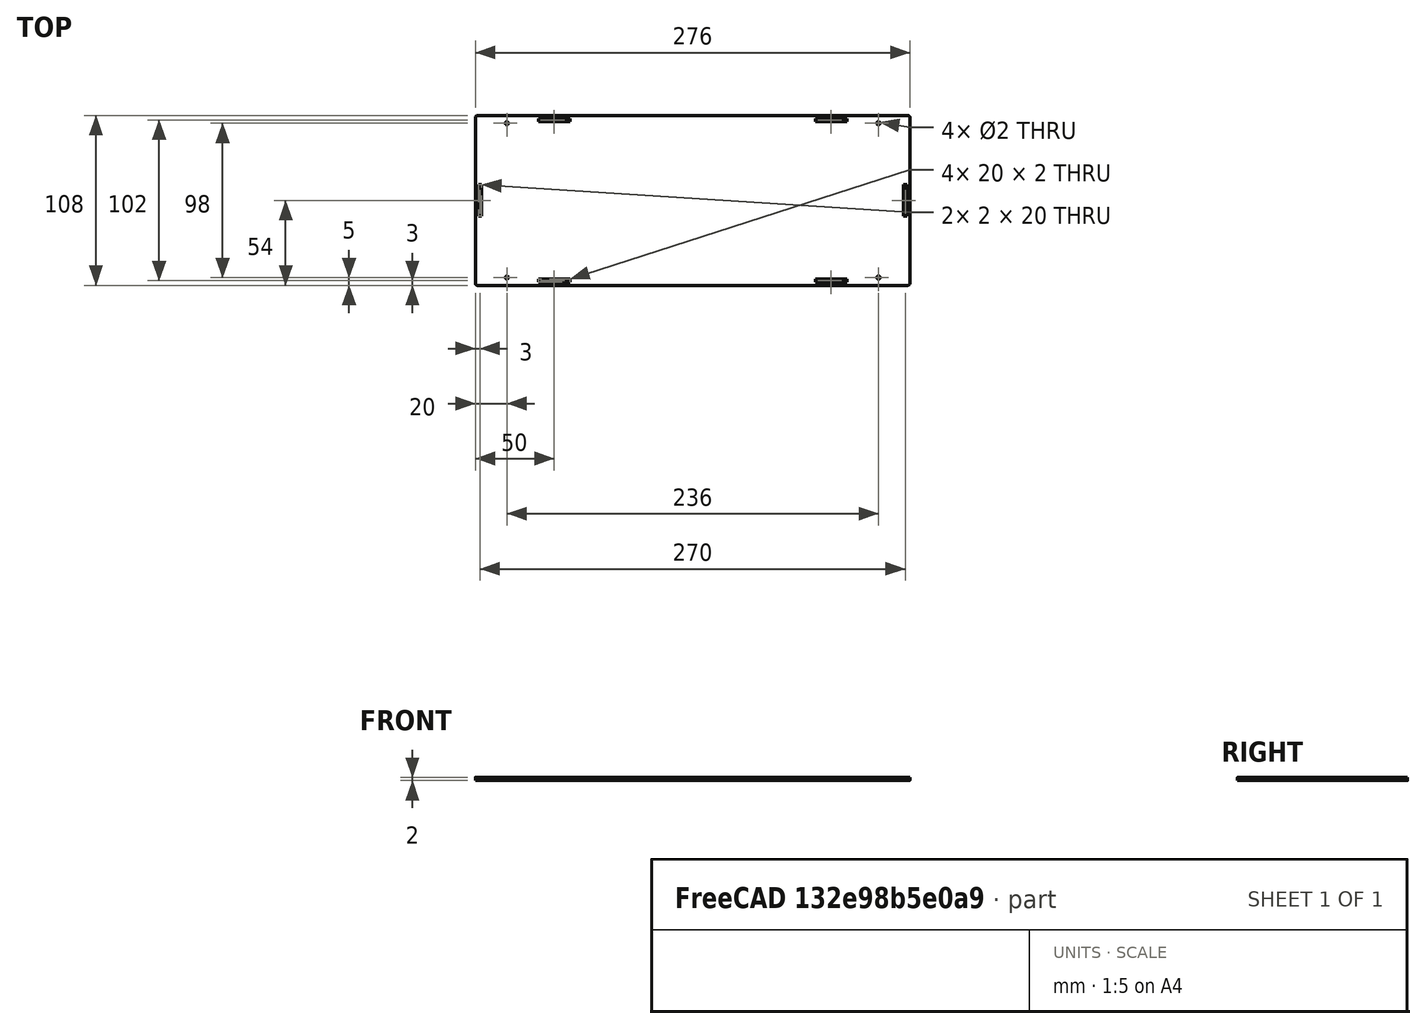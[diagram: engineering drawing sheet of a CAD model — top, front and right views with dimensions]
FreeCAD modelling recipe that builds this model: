
FCSTD DOCUMENT  (FreeCAD 0.19R24291 (Git))
Label: keyboard-pc
License: All rights reserved
LicenseURL: http://en.wikipedia.org/wiki/All_rights_reserved
objects: Sketcher::SketchObject×1, PartDesign::Pad×1, PartDesign::Body×1
note: 4 computed .brp shape members not serialized (recipe doc carries the construction recipe); baked Part::Feature solids carry a one-line shape summary decoded from their .brp

FEATURE [Sketcher::SketchObject] Sketch  label="keyboard-up"
  FullyConstrained = false
  MapMode = 5
  Support = -> [XY_Plane]
  sketch-geometry (176):
    g0: LineSegment StartX=-136.5 StartY=54 StartZ=0 EndX=136.5 EndY=54 EndZ=0
    g1: LineSegment StartX=138 StartY=52.5 StartZ=0 EndX=138 EndY=-52.5 EndZ=0
    g2: LineSegment StartX=136.5 StartY=-54 StartZ=0 EndX=-136.5 EndY=-54 EndZ=0
    g3: LineSegment StartX=-138 StartY=-52.5 StartZ=0 EndX=-138 EndY=52.5 EndZ=0
    g4: Circle CenterX=-118 CenterY=-49 CenterZ=0 NormalX=0 NormalY=0 NormalZ=1 AngleXU=0 Radius=1
    g5: Circle CenterX=118 CenterY=-49 CenterZ=0 NormalX=0 NormalY=0 NormalZ=1 AngleXU=0 Radius=1
    g6: Circle CenterX=-118 CenterY=49 CenterZ=0 NormalX=0 NormalY=0 NormalZ=1 AngleXU=0 Radius=1
    g7: Circle CenterX=118 CenterY=49 CenterZ=0 NormalX=0 NormalY=0 NormalZ=1 AngleXU=0 Radius=1
    g8: LineSegment StartX=-98 StartY=-50 StartZ=0 EndX=-78 EndY=-50 EndZ=0
    g9: LineSegment StartX=-78 StartY=-50 StartZ=0 EndX=-78 EndY=-52 EndZ=0
    g10: LineSegment StartX=-78 StartY=-52 StartZ=0 EndX=-98 EndY=-52 EndZ=0
    g11: LineSegment StartX=-98 StartY=-52 StartZ=0 EndX=-98 EndY=-50 EndZ=0
    g12: LineSegment StartX=-98 StartY=52 StartZ=0 EndX=-78 EndY=52 EndZ=0
    g13: LineSegment StartX=-78 StartY=52 StartZ=0 EndX=-78 EndY=50 EndZ=0
    g14: LineSegment StartX=-78 StartY=50 StartZ=0 EndX=-98 EndY=50 EndZ=0
    g15: LineSegment StartX=-98 StartY=50 StartZ=0 EndX=-98 EndY=52 EndZ=0
    g16: LineSegment StartX=78 StartY=52 StartZ=0 EndX=98 EndY=52 EndZ=0
    g17: LineSegment StartX=98 StartY=52 StartZ=0 EndX=98 EndY=50 EndZ=0
    g18: LineSegment StartX=98 StartY=50 StartZ=0 EndX=78 EndY=50 EndZ=0
    g19: LineSegment StartX=78 StartY=50 StartZ=0 EndX=78 EndY=52 EndZ=0
    g20: LineSegment StartX=78 StartY=-50 StartZ=0 EndX=98 EndY=-50 EndZ=0
    g21: LineSegment StartX=98 StartY=-50 StartZ=0 EndX=98 EndY=-52 EndZ=0
    g22: LineSegment StartX=98 StartY=-52 StartZ=0 EndX=78 EndY=-52 EndZ=0
    g23: LineSegment StartX=78 StartY=-52 StartZ=0 EndX=78 EndY=-50 EndZ=0
    g24: LineSegment StartX=-136 StartY=10 StartZ=0 EndX=-134 EndY=10 EndZ=0
    g25: LineSegment StartX=-134 StartY=10 StartZ=0 EndX=-134 EndY=-10 EndZ=0
    g26: LineSegment StartX=-134 StartY=-10 StartZ=0 EndX=-136 EndY=-10 EndZ=0
    g27: LineSegment StartX=-136 StartY=-10 StartZ=0 EndX=-136 EndY=10 EndZ=0
    g28: LineSegment StartX=134 StartY=10 StartZ=0 EndX=136 EndY=10 EndZ=0
    g29: LineSegment StartX=136 StartY=10 StartZ=0 EndX=136 EndY=-10 EndZ=0
    g30: LineSegment StartX=136 StartY=-10 StartZ=0 EndX=134 EndY=-10 EndZ=0
    g31: LineSegment StartX=134 StartY=-10 StartZ=0 EndX=134 EndY=10 EndZ=0
    g32: ArcOfCircle CenterX=-136.5 CenterY=-52.5 CenterZ=0 NormalX=0 NormalY=0 NormalZ=1 AngleXU=0 Radius=1.5 StartAngle=3.14159 EndAngle=4.71239
    g33: ArcOfCircle CenterX=-136.5 CenterY=52.5 CenterZ=0 NormalX=0 NormalY=0 NormalZ=1 AngleXU=0 Radius=1.5 StartAngle=1.5708 EndAngle=3.14159
    g34: ArcOfCircle CenterX=136.5 CenterY=52.5 CenterZ=0 NormalX=0 NormalY=0 NormalZ=1 AngleXU=0 Radius=1.5 StartAngle=-1.8e-15 EndAngle=1.5708
    g35: ArcOfCircle CenterX=136.5 CenterY=-52.5 CenterZ=0 NormalX=0 NormalY=0 NormalZ=1 AngleXU=0 Radius=1.5 StartAngle=4.71239 EndAngle=6.28319
    g36: LineSegment StartX=-118 StartY=44 StartZ=0 EndX=-82 EndY=44 EndZ=0
    g37: LineSegment StartX=-82 StartY=44 StartZ=0 EndX=-82 EndY=42 EndZ=0
    g38: LineSegment StartX=-82 StartY=42 StartZ=0 EndX=-118 EndY=42 EndZ=0
    g39: LineSegment StartX=-118 StartY=42 StartZ=0 EndX=-118 EndY=44 EndZ=0
    g40: Circle CenterX=44 CenterY=30.5 CenterZ=0 NormalX=0 NormalY=0 NormalZ=1 AngleXU=0 Radius=1.5
    g41: Circle CenterX=44 CenterY=-30.5 CenterZ=0 NormalX=0 NormalY=0 NormalZ=1 AngleXU=0 Radius=1.5
    g42: Circle CenterX=120 CenterY=30.5 CenterZ=0 NormalX=0 NormalY=0 NormalZ=1 AngleXU=0 Radius=1.5
    g43: Circle CenterX=120 CenterY=-30.5 CenterZ=0 NormalX=0 NormalY=0 NormalZ=1 AngleXU=0 Radius=1.5
    g44: Circle CenterX=34 CenterY=30.5 CenterZ=0 NormalX=0 NormalY=0 NormalZ=1 AngleXU=0 Radius=1.5
    g45: Circle CenterX=34 CenterY=-30.5 CenterZ=0 NormalX=0 NormalY=0 NormalZ=1 AngleXU=0 Radius=1.5
    g46: Circle CenterX=110 CenterY=30.5 CenterZ=0 NormalX=0 NormalY=0 NormalZ=1 AngleXU=0 Radius=1.5
    g47: Circle CenterX=110 CenterY=-30.5 CenterZ=0 NormalX=0 NormalY=0 NormalZ=1 AngleXU=0 Radius=1.5
    g48: Circle CenterX=-111.5 CenterY=-48.5 CenterZ=0 NormalX=0 NormalY=0 NormalZ=1 AngleXU=0 Radius=1.5
    g49: Circle CenterX=-111.5 CenterY=48.5 CenterZ=0 NormalX=0 NormalY=0 NormalZ=1 AngleXU=0 Radius=1.5
    g50: Circle CenterX=111.5 CenterY=-48.5 CenterZ=0 NormalX=0 NormalY=0 NormalZ=1 AngleXU=0 Radius=1.5
    g51: Circle CenterX=111.5 CenterY=48.5 CenterZ=0 NormalX=0 NormalY=0 NormalZ=1 AngleXU=0 Radius=1.5
    g52: Circle CenterX=-130 CenterY=-39 CenterZ=0 NormalX=0 NormalY=0 NormalZ=1 AngleXU=0 Radius=1
    g53: Circle CenterX=7.5 CenterY=-37 CenterZ=0 NormalX=0 NormalY=0 NormalZ=1 AngleXU=0 Radius=1
    g54: Circle CenterX=-128 CenterY=21 CenterZ=0 NormalX=0 NormalY=0 NormalZ=1 AngleXU=0 Radius=1
    g55: Circle CenterX=-43.5 CenterY=32 CenterZ=0 NormalX=0 NormalY=0 NormalZ=1 AngleXU=0 Radius=1.5
    g56: ArcOfCircle CenterX=-112.237 CenterY=33 CenterZ=0 NormalX=0 NormalY=0 NormalZ=1 AngleXU=0 Radius=1.5 StartAngle=5e-16 EndAngle=3.14159
    g57: ArcOfCircle CenterX=-112.237 CenterY=-33 CenterZ=0 NormalX=0 NormalY=0 NormalZ=1 AngleXU=0 Radius=1.5 StartAngle=3.14159 EndAngle=6.28319
    g58: LineSegment StartX=-113.737 StartY=33 StartZ=0 EndX=-113.737 EndY=-33 EndZ=0
    g59: LineSegment StartX=-110.737 StartY=33 StartZ=0 EndX=-110.737 EndY=-33 EndZ=0
    g60: ArcOfCircle CenterX=-106.237 CenterY=33 CenterZ=0 NormalX=0 NormalY=0 NormalZ=1 AngleXU=0 Radius=1.5 StartAngle=5e-16 EndAngle=3.14159
    g61: ArcOfCircle CenterX=-106.237 CenterY=-33 CenterZ=0 NormalX=0 NormalY=0 NormalZ=1 AngleXU=0 Radius=1.5 StartAngle=3.14159 EndAngle=6.28319
    g62: LineSegment StartX=-107.737 StartY=33 StartZ=0 EndX=-107.737 EndY=-33 EndZ=0
    g63: LineSegment StartX=-104.737 StartY=33 StartZ=0 EndX=-104.737 EndY=-33 EndZ=0
    g64: ArcOfCircle CenterX=-94.2366 CenterY=33 CenterZ=0 NormalX=0 NormalY=0 NormalZ=1 AngleXU=0 Radius=1.5 StartAngle=0 EndAngle=3.14159
    g65: ArcOfCircle CenterX=-94.2366 CenterY=-33 CenterZ=0 NormalX=0 NormalY=0 NormalZ=1 AngleXU=0 Radius=1.5 StartAngle=3.14159 EndAngle=6.28319
    g66: LineSegment StartX=-95.7366 StartY=33 StartZ=0 EndX=-95.7366 EndY=-33 EndZ=0
    g67: LineSegment StartX=-92.7366 StartY=33 StartZ=0 EndX=-92.7366 EndY=-33 EndZ=0
    g68: ArcOfCircle CenterX=-88.2366 CenterY=33 CenterZ=0 NormalX=0 NormalY=0 NormalZ=1 AngleXU=0 Radius=1.5 StartAngle=5e-16 EndAngle=3.14159
    g69: ArcOfCircle CenterX=-88.2366 CenterY=-33 CenterZ=0 NormalX=0 NormalY=0 NormalZ=1 AngleXU=0 Radius=1.5 StartAngle=3.14159 EndAngle=6.28319
    g70: LineSegment StartX=-89.7366 StartY=33 StartZ=0 EndX=-89.7366 EndY=-33 EndZ=0
    g71: LineSegment StartX=-86.7366 StartY=33 StartZ=0 EndX=-86.7366 EndY=-33 EndZ=0
    g72: ArcOfCircle CenterX=-76.2366 CenterY=33 CenterZ=0 NormalX=0 NormalY=0 NormalZ=1 AngleXU=0 Radius=1.5 StartAngle=2.2e-15 EndAngle=3.14159
    g73: ArcOfCircle CenterX=-76.2366 CenterY=-33 CenterZ=0 NormalX=0 NormalY=0 NormalZ=1 AngleXU=0 Radius=1.5 StartAngle=3.14159 EndAngle=6.28319
    g74: LineSegment StartX=-77.7366 StartY=33 StartZ=0 EndX=-77.7366 EndY=-33 EndZ=0
    g75: LineSegment StartX=-74.7366 StartY=33 StartZ=0 EndX=-74.7366 EndY=-33 EndZ=0
    g76: ArcOfCircle CenterX=-70.2366 CenterY=33 CenterZ=0 NormalX=0 NormalY=0 NormalZ=1 AngleXU=0 Radius=1.5 StartAngle=5e-16 EndAngle=3.14159
    g77: ArcOfCircle CenterX=-70.2366 CenterY=-33 CenterZ=0 NormalX=0 NormalY=0 NormalZ=1 AngleXU=0 Radius=1.5 StartAngle=3.14159 EndAngle=6.28319
    g78: LineSegment StartX=-71.7366 StartY=33 StartZ=0 EndX=-71.7366 EndY=-33 EndZ=0
    g79: LineSegment StartX=-68.7366 StartY=33 StartZ=0 EndX=-68.7366 EndY=-33 EndZ=0
    g80: ArcOfCircle CenterX=-58.2366 CenterY=33 CenterZ=0 NormalX=0 NormalY=0 NormalZ=1 AngleXU=0 Radius=1.5 StartAngle=0 EndAngle=3.14159
    g81: ArcOfCircle CenterX=-58.2366 CenterY=-33 CenterZ=0 NormalX=0 NormalY=0 NormalZ=1 AngleXU=0 Radius=1.5 StartAngle=3.14159 EndAngle=6.28319
    g82: LineSegment StartX=-59.7366 StartY=33 StartZ=0 EndX=-59.7366 EndY=-33 EndZ=0
    g83: LineSegment StartX=-56.7366 StartY=33 StartZ=0 EndX=-56.7366 EndY=-33 EndZ=0
    g84: ArcOfCircle CenterX=-52.2366 CenterY=33 CenterZ=0 NormalX=0 NormalY=0 NormalZ=1 AngleXU=0 Radius=1.5 StartAngle=1.9e-15 EndAngle=3.14159
    g85: ArcOfCircle CenterX=-52.2366 CenterY=-33 CenterZ=0 NormalX=0 NormalY=0 NormalZ=1 AngleXU=0 Radius=1.5 StartAngle=3.14159 EndAngle=6.28319
    g86: LineSegment StartX=-53.7366 StartY=33 StartZ=0 EndX=-53.7366 EndY=-33 EndZ=0
    g87: LineSegment StartX=-50.7366 StartY=33 StartZ=0 EndX=-50.7366 EndY=-33 EndZ=0
    g88: ArcOfCircle CenterX=-40.2366 CenterY=33 CenterZ=0 NormalX=0 NormalY=0 NormalZ=1 AngleXU=0 Radius=1.5 StartAngle=1.9e-15 EndAngle=3.14159
    g89: ArcOfCircle CenterX=-40.2366 CenterY=-33 CenterZ=0 NormalX=0 NormalY=0 NormalZ=1 AngleXU=0 Radius=1.5 StartAngle=3.14159 EndAngle=6.28319
    g90: LineSegment StartX=-41.7366 StartY=33 StartZ=0 EndX=-41.7366 EndY=-33 EndZ=0
    g91: LineSegment StartX=-38.7366 StartY=33 StartZ=0 EndX=-38.7366 EndY=-33 EndZ=0
    g92: ArcOfCircle CenterX=-34.2366 CenterY=33 CenterZ=0 NormalX=0 NormalY=0 NormalZ=1 AngleXU=0 Radius=1.5 StartAngle=-1.8e-15 EndAngle=3.14159
    g93: ArcOfCircle CenterX=-34.2366 CenterY=-33 CenterZ=0 NormalX=0 NormalY=0 NormalZ=1 AngleXU=0 Radius=1.5 StartAngle=3.14159 EndAngle=6.28319
    g94: LineSegment StartX=-35.7366 StartY=33 StartZ=0 EndX=-35.7366 EndY=-33 EndZ=0
    g95: LineSegment StartX=-32.7366 StartY=33 StartZ=0 EndX=-32.7366 EndY=-33 EndZ=0
    g96: ArcOfCircle CenterX=-22.2366 CenterY=33 CenterZ=0 NormalX=0 NormalY=0 NormalZ=1 AngleXU=0 Radius=1.5 StartAngle=2.3e-15 EndAngle=3.14159
    g97: ArcOfCircle CenterX=-22.2366 CenterY=-33 CenterZ=0 NormalX=0 NormalY=0 NormalZ=1 AngleXU=0 Radius=1.5 StartAngle=3.14159 EndAngle=6.28319
    g98: LineSegment StartX=-23.7366 StartY=33 StartZ=0 EndX=-23.7366 EndY=-33 EndZ=0
    g99: LineSegment StartX=-20.7366 StartY=33 StartZ=0 EndX=-20.7366 EndY=-33 EndZ=0
    g100: ArcOfCircle CenterX=-16.2366 CenterY=33 CenterZ=0 NormalX=0 NormalY=0 NormalZ=1 AngleXU=0 Radius=1.5 StartAngle=3.6e-15 EndAngle=3.14159
    g101: ArcOfCircle CenterX=-16.2366 CenterY=-33 CenterZ=0 NormalX=0 NormalY=0 NormalZ=1 AngleXU=0 Radius=1.5 StartAngle=3.14159 EndAngle=6.28319
    g102: LineSegment StartX=-17.7366 StartY=33 StartZ=0 EndX=-17.7366 EndY=-33 EndZ=0
    g103: LineSegment StartX=-14.7366 StartY=33 StartZ=0 EndX=-14.7366 EndY=-33 EndZ=0
    g104: ArcOfCircle CenterX=65.2339 CenterY=33 CenterZ=0 NormalX=0 NormalY=0 NormalZ=1 AngleXU=0 Radius=1.5 StartAngle=7e-16 EndAngle=3.14159
    g105: ArcOfCircle CenterX=65.2339 CenterY=-33 CenterZ=0 NormalX=0 NormalY=0 NormalZ=1 AngleXU=0 Radius=1.5 StartAngle=3.14159 EndAngle=6.28319
    g106: LineSegment StartX=63.7339 StartY=33 StartZ=0 EndX=63.7339 EndY=-33 EndZ=0
    g107: LineSegment StartX=66.7339 StartY=33 StartZ=0 EndX=66.7339 EndY=-33 EndZ=0
    g108: ArcOfCircle CenterX=71.2339 CenterY=33 CenterZ=0 NormalX=0 NormalY=0 NormalZ=1 AngleXU=0 Radius=1.5 StartAngle=9e-16 EndAngle=3.14159
    g109: ArcOfCircle CenterX=71.2339 CenterY=-33 CenterZ=0 NormalX=0 NormalY=0 NormalZ=1 AngleXU=0 Radius=1.5 StartAngle=3.14159 EndAngle=6.28319
    g110: LineSegment StartX=69.7339 StartY=33 StartZ=0 EndX=69.7339 EndY=-33 EndZ=0
    g111: LineSegment StartX=72.7339 StartY=33 StartZ=0 EndX=72.7339 EndY=-33 EndZ=0
    g112: ArcOfCircle CenterX=83.2339 CenterY=33 CenterZ=0 NormalX=0 NormalY=0 NormalZ=1 AngleXU=0 Radius=1.5 StartAngle=1.7e-15 EndAngle=3.14159
    g113: ArcOfCircle CenterX=83.2339 CenterY=-33 CenterZ=0 NormalX=0 NormalY=0 NormalZ=1 AngleXU=0 Radius=1.5 StartAngle=3.14159 EndAngle=6.28319
    g114: LineSegment StartX=81.7339 StartY=33 StartZ=0 EndX=81.7339 EndY=-33 EndZ=0
    g115: LineSegment StartX=84.7339 StartY=33 StartZ=0 EndX=84.7339 EndY=-33 EndZ=0
    g116: ArcOfCircle CenterX=89.2339 CenterY=33 CenterZ=0 NormalX=0 NormalY=0 NormalZ=1 AngleXU=0 Radius=1.5 StartAngle=6e-16 EndAngle=3.14159
    g117: ArcOfCircle CenterX=89.2339 CenterY=-33 CenterZ=0 NormalX=0 NormalY=0 NormalZ=1 AngleXU=0 Radius=1.5 StartAngle=3.14159 EndAngle=6.28319
    g118: LineSegment StartX=87.7339 StartY=33 StartZ=0 EndX=87.7339 EndY=-33 EndZ=0
    g119: LineSegment StartX=90.7339 StartY=33 StartZ=0 EndX=90.7339 EndY=-33 EndZ=0
    g120: LineSegment StartX=-156.5 StartY=50 StartZ=0 EndX=-146.5 EndY=50 EndZ=0
    g121: LineSegment StartX=-146.5 StartY=50 StartZ=0 EndX=-146.5 EndY=-50 EndZ=0
    g122: LineSegment StartX=-146.5 StartY=-50 StartZ=0 EndX=-156.5 EndY=-50 EndZ=0
    g123: LineSegment StartX=-156.5 StartY=-50 StartZ=0 EndX=-156.5 EndY=50 EndZ=0
    g124: LineSegment StartX=-146.5 StartY=10 StartZ=0 EndX=-144.5 EndY=10 EndZ=0
    g125: LineSegment StartX=-144.5 StartY=10 StartZ=0 EndX=-144.5 EndY=-10 EndZ=0
    g126: LineSegment StartX=-144.5 StartY=-10 StartZ=0 EndX=-146.5 EndY=-10 EndZ=0
    g127: LineSegment StartX=-146.5 StartY=-10 StartZ=0 EndX=-146.5 EndY=10 EndZ=0
    g128: LineSegment StartX=-158.5 StartY=10 StartZ=0 EndX=-156.5 EndY=10 EndZ=0
    g129: LineSegment StartX=-156.5 StartY=10 StartZ=0 EndX=-156.5 EndY=-10 EndZ=0
    g130: LineSegment StartX=-156.5 StartY=-10 StartZ=0 EndX=-158.5 EndY=-10 EndZ=0
    g131: LineSegment StartX=-158.5 StartY=-10 StartZ=0 EndX=-158.5 EndY=10 EndZ=0
    g132: LineSegment StartX=-154 StartY=-50 StartZ=0 EndX=-149 EndY=-50 EndZ=0
    g133: LineSegment StartX=-149 StartY=-50 StartZ=0 EndX=-149 EndY=-52 EndZ=0
    g134: LineSegment StartX=-149 StartY=-52 StartZ=0 EndX=-154 EndY=-52 EndZ=0
    g135: LineSegment StartX=-154 StartY=-52 StartZ=0 EndX=-154 EndY=-50 EndZ=0
    g136: LineSegment StartX=-154 StartY=52 StartZ=0 EndX=-149 EndY=52 EndZ=0
    g137: LineSegment StartX=-149 StartY=52 StartZ=0 EndX=-149 EndY=50 EndZ=0
    g138: LineSegment StartX=-149 StartY=50 StartZ=0 EndX=-154 EndY=50 EndZ=0
    g139: LineSegment StartX=-154 StartY=50 StartZ=0 EndX=-154 EndY=52 EndZ=0
    g140: LineSegment StartX=-138 StartY=72.5 StartZ=0 EndX=138 EndY=72.5 EndZ=0
    g141: LineSegment StartX=138 StartY=72.5 StartZ=0 EndX=138 EndY=62.5 EndZ=0
    g142: LineSegment StartX=138 StartY=62.5 StartZ=0 EndX=-138 EndY=62.5 EndZ=0
    g143: LineSegment StartX=-138 StartY=62.5 StartZ=0 EndX=-138 EndY=72.5 EndZ=0
    g144: LineSegment StartX=-136 StartY=70 StartZ=0 EndX=-134 EndY=70 EndZ=0
    g145: LineSegment StartX=-134 StartY=70 StartZ=0 EndX=-134 EndY=65 EndZ=0
    g146: LineSegment StartX=-134 StartY=65 StartZ=0 EndX=-136 EndY=65 EndZ=0
    g147: LineSegment StartX=-136 StartY=65 StartZ=0 EndX=-136 EndY=70 EndZ=0
    g148: LineSegment StartX=-98 StartY=62.5 StartZ=0 EndX=-78 EndY=62.5 EndZ=0
    g149: LineSegment StartX=-78 StartY=62.5 StartZ=0 EndX=-78 EndY=60.5 EndZ=0
    g150: LineSegment StartX=-78 StartY=60.5 StartZ=0 EndX=-98 EndY=60.5 EndZ=0
    g151: LineSegment StartX=-98 StartY=60.5 StartZ=0 EndX=-98 EndY=62.5 EndZ=0
    g152: LineSegment StartX=-98 StartY=74.5 StartZ=0 EndX=-78 EndY=74.5 EndZ=0
    g153: LineSegment StartX=-78 StartY=74.5 StartZ=0 EndX=-78 EndY=72.5 EndZ=0
    g154: LineSegment StartX=-78 StartY=72.5 StartZ=0 EndX=-98 EndY=72.5 EndZ=0
    g155: LineSegment StartX=-98 StartY=72.5 StartZ=0 EndX=-98 EndY=74.5 EndZ=0
    g156: LineSegment StartX=134 StartY=70 StartZ=0 EndX=136 EndY=70 EndZ=0
    g157: LineSegment StartX=136 StartY=70 StartZ=0 EndX=136 EndY=65 EndZ=0
    g158: LineSegment StartX=136 StartY=65 StartZ=0 EndX=134 EndY=65 EndZ=0
    g159: LineSegment StartX=134 StartY=65 StartZ=0 EndX=134 EndY=70 EndZ=0
    g160: LineSegment StartX=78 StartY=74.5 StartZ=0 EndX=98 EndY=74.5 EndZ=0
    g161: LineSegment StartX=98 StartY=74.5 StartZ=0 EndX=98 EndY=72.5 EndZ=0
    g162: LineSegment StartX=98 StartY=72.5 StartZ=0 EndX=78 EndY=72.5 EndZ=0
    g163: LineSegment StartX=78 StartY=72.5 StartZ=0 EndX=78 EndY=74.5 EndZ=0
    g164: LineSegment StartX=78 StartY=62.5 StartZ=0 EndX=98 EndY=62.5 EndZ=0
    g165: LineSegment StartX=98 StartY=62.5 StartZ=0 EndX=98 EndY=60.5 EndZ=0
    g166: LineSegment StartX=98 StartY=60.5 StartZ=0 EndX=78 EndY=60.5 EndZ=0
    g167: LineSegment StartX=78 StartY=60.5 StartZ=0 EndX=78 EndY=62.5 EndZ=0
    g168: LineSegment StartX=-151.5 StartY=14.5 StartZ=0 EndX=-147.5 EndY=14.5 EndZ=0
    g169: LineSegment StartX=-147.5 StartY=14.5 StartZ=0 EndX=-147.5 EndY=-40 EndZ=0
    g170: LineSegment StartX=-147.5 StartY=-40 StartZ=0 EndX=-151.5 EndY=-40 EndZ=0
    g171: LineSegment StartX=-151.5 StartY=-40 StartZ=0 EndX=-151.5 EndY=14.5 EndZ=0
    g172: LineSegment StartX=-153.5 StartY=8 StartZ=0 EndX=-151.5 EndY=8 EndZ=0
    g173: LineSegment StartX=-151.5 StartY=8 StartZ=0 EndX=-151.5 EndY=-35 EndZ=0
    g174: LineSegment StartX=-151.5 StartY=-35 StartZ=0 EndX=-153.5 EndY=-35 EndZ=0
    g175: LineSegment StartX=-153.5 StartY=-35 StartZ=0 EndX=-153.5 EndY=8 EndZ=0
  constraints (462):
    c: Horizontal(g2)
    c: Vertical(g1)
    c: Diameter(g4) = 2
    c: Diameter(g5) = 2
    c: Diameter(g6) = 2
    c: Diameter(g7) = 2
    c: Coincident(g8,g9)
    c: Coincident(g9,g10)
    c: Coincident(g10,g11)
    c: Coincident(g11,g8)
    c: Horizontal(g8)
    c: Horizontal(g10)
    c: Vertical(g9)
    c: Vertical(g11)
    c: DistanceX(g8,g8) = 20
    c: DistanceY(g9,g9) = 2
    c: Coincident(g12,g13)
    c: Coincident(g13,g14)
    c: Coincident(g14,g15)
    c: Coincident(g15,g12)
    c: Horizontal(g12)
    c: Horizontal(g14)
    c: Vertical(g13)
    c: Vertical(g15)
    c: Coincident(g16,g17)
    c: Coincident(g17,g18)
    c: Coincident(g18,g19)
    c: Coincident(g19,g16)
    c: Horizontal(g16)
    c: Horizontal(g18)
    c: Vertical(g17)
    c: Vertical(g19)
    c: Coincident(g20,g21)
    c: Coincident(g21,g22)
    c: Coincident(g22,g23)
    c: Coincident(g23,g20)
    c: Horizontal(g20)
    c: Horizontal(g22)
    c: Vertical(g21)
    c: Vertical(g23)
    c: DistanceX(g12,g12) = 20
    c: DistanceX(g16,g16) = 20
    c: DistanceX(g20,g20) = 20
    c: DistanceY(g13,g13) = 2
    c: DistanceY(g17,g17) = 2
    c: DistanceY(g21,g21) = 2
    c: Coincident(g24,g25)
    c: Coincident(g25,g26)
    c: Coincident(g26,g27)
    c: Coincident(g27,g24)
    c: Horizontal(g24)
    c: Horizontal(g26)
    c: Vertical(g27)
    c: Coincident(g28,g29)
    c: Coincident(g29,g30)
    c: Coincident(g30,g31)
    c: Coincident(g31,g28)
    c: Horizontal(g28)
    c: Horizontal(g30)
    c: Vertical(g31)
    c: DistanceX(g24,g24) = 2
    c: DistanceX(g28,g28) = 2
    c: DistanceY(g25,g25) = 20
    c: DistanceY(g29,g29) = 20
    c: Symmetric(g24,g25,g-1)
    c: Symmetric(g28,g29,g-1)
    c: Tangent(g2,g32) = 1.5708
    c: Tangent(g3,g32) = 1.5708
    c: Radius(g32) = 1.5
    c: Tangent(g0,g33) = 1.5708
    c: Tangent(g3,g33) = 1.5708
    c: Radius(g33) = 1.5
    c: DistanceX(g-1,g30) = 134
    c: DistanceX(g25,g-1) = 134
    c: DistanceX(g33,g24) = 0.5
    c: DistanceY(g32,g10) = 0.5
    c: DistanceX(g32,g10) = 38.5
    c: DistanceX(g32,g4) = 18.5
    c: DistanceY(g32,g4) = 3.5
    c: DistanceX(g33,g6) = 18.5
    c: DistanceY(g12,g33) = 0.5
    c: DistanceX(g33,g12) = 38.5
    c: DistanceY(g6,g33) = 3.5
    c: Tangent(g0,g34) = 1.5708
    c: Tangent(g1,g34) = 1.5708
    c: Tangent(g1,g35) = 1.5708
    c: Tangent(g2,g35) = 1.5708
    c: Symmetric(g34,g35,g-1)
    c: Symmetric(g35,g32,g-2)
    c: Symmetric(g34,g33,g-2)
    c: DistanceY(g35,g34) = 105
    c: DistanceY(g16,g34) = 0.5
    c: DistanceX(g16,g34) = 38.5
    c: DistanceY(g7,g34) = 3.5
    c: DistanceX(g7,g34) = 18.5
    c: DistanceY(g35,g5) = 3.5
    c: DistanceX(g5,g35) = 18.5
    c: DistanceX(g21,g35) = 38.5
    c: DistanceY(g35,g21) = 0.5
    c: Coincident(g36,g37)
    c: Coincident(g37,g38)
    c: Coincident(g38,g39)
    c: Coincident(g39,g36)
    c: Horizontal(g36)
    c: Horizontal(g38)
    c: Vertical(g37)
    c: Vertical(g39)
    c: DistanceY(g37,g37) = 2
    c: DistanceX(g38,g38) = 36
    c: DistanceX(g33,g36) = 18.5
    c: DistanceY(g36,g33) = 8.5
    c: Diameter(g40) = 3
    c: Diameter(g41) = 3
    c: DistanceY(g41,g40) = 61
    c: Diameter(g42) = 3
    c: Diameter(g43) = 3
    c: DistanceY(g43,g42) = 61
    c: DistanceX(g40,g42) = 76
    c: Symmetric(g41,g40,g-1)
    c: Symmetric(g43,g42,g-1)
    c: DistanceX(g42,g28) = 14
    c: Diameter(g44) = 3
    c: Diameter(g45) = 3
    c: DistanceY(g45,g44) = 61
    c: Diameter(g46) = 3
    c: Diameter(g47) = 3
    c: DistanceY(g47,g46) = 61
    c: DistanceX(g44,g46) = 76
    c: Symmetric(g46,g47,g-1)
    c: DistanceX(g46,g42) = 10
    c: Diameter(g48) = 3
    c: DistanceX(g32,g48) = 25
    c: DistanceY(g32,g48) = 4
    c: Diameter(g49) = 3
    c: DistanceY(g49,g33) = 4
    c: DistanceX(g33,g49) = 25
    c: Symmetric(g45,g44,g-1)
    c: Diameter(g50) = 3
    c: DistanceX(g50,g35) = 25
    c: DistanceY(g35,g50) = 4
    c: Diameter(g51) = 3
    c: DistanceX(g51,g34) = 25
    c: DistanceY(g51,g34) = 4
    c: Diameter(g52) = 2
    c: DistanceY(g32,g52) = 13.5
    c: DistanceX(g32,g52) = 6.5
    c: Diameter(g53) = 2
    c: DistanceX(g52,g53) = 137.5
    c: DistanceY(g32,g53) = 15.5
    c: Diameter(g54) = 2
    c: DistanceX(g24,g54) = 8
    c: Diameter(g55) = 3
    c: DistanceY(g8,g55) = 82
    c: DistanceX(g54,g55) = 84.5
    c: Tangent(g56,g59) = 1.5708
    c: Tangent(g56,g58) = -1.5708
    c: Tangent(g58,g57) = -1.5708
    c: Tangent(g59,g57) = 1.5708
    c: Vertical(g58)
    c: DistanceY(g57,g56) = 66
    c: Symmetric(g57,g56,g-1)
    c: DistanceX(g57,g57) = 3
    c: Tangent(g60,g63) = 1.5708
    c: Tangent(g60,g62) = -1.5708
    c: Tangent(g62,g61) = -1.5708
    c: Tangent(g63,g61) = 1.5708
    c: Vertical(g62)
    c: DistanceY(g61,g60) = 66
    c: DistanceX(g61,g61) = 3
    c: Symmetric(g60,g61,g-1)
    c: DistanceX(g56,g60) = 6
    c: Tangent(g64,g67) = 1.5708
    c: Tangent(g64,g66) = -1.5708
    c: Tangent(g66,g65) = -1.5708
    c: Tangent(g67,g65) = 1.5708
    c: Vertical(g66)
    c: DistanceY(g65,g64) = 66
    c: DistanceX(g65,g65) = 3
    c: Tangent(g68,g71) = 1.5708
    c: Tangent(g68,g70) = -1.5708
    c: Tangent(g70,g69) = -1.5708
    c: Tangent(g71,g69) = 1.5708
    c: Vertical(g70)
    c: DistanceY(g69,g68) = 66
    c: DistanceX(g69,g69) = 3
    c: DistanceX(g64,g68) = 6
    c: Symmetric(g64,g65,g-1)
    c: Symmetric(g68,g69,g-1)
    c: DistanceX(g60,g64) = 12
    c: Tangent(g72,g75) = 1.5708
    c: Tangent(g72,g74) = -1.5708
    c: Tangent(g74,g73) = -1.5708
    c: Tangent(g75,g73) = 1.5708
    c: Vertical(g74)
    c: DistanceY(g73,g72) = 66
    c: DistanceX(g73,g73) = 3
    c: Tangent(g76,g79) = 1.5708
    c: Tangent(g76,g78) = -1.5708
    c: Tangent(g78,g77) = -1.5708
    c: Tangent(g79,g77) = 1.5708
    c: Vertical(g78)
    c: DistanceY(g77,g76) = 66
    c: DistanceX(g77,g77) = 3
    c: DistanceX(g72,g76) = 6
    c: Tangent(g80,g83) = 1.5708
    c: Tangent(g80,g82) = -1.5708
    c: Tangent(g82,g81) = -1.5708
    c: Tangent(g83,g81) = 1.5708
    c: Vertical(g82)
    c: DistanceY(g81,g80) = 66
    c: DistanceX(g81,g81) = 3
    c: Tangent(g84,g87) = 1.5708
    c: Tangent(g84,g86) = -1.5708
    c: Tangent(g86,g85) = -1.5708
    c: Tangent(g87,g85) = 1.5708
    c: Vertical(g86)
    c: DistanceY(g85,g84) = 66
    c: DistanceX(g85,g85) = 3
    c: DistanceX(g80,g84) = 6
    c: DistanceX(g76,g80) = 12
    c: DistanceX(g68,g72) = 12
    c: Tangent(g88,g91) = 1.5708
    c: Tangent(g88,g90) = -1.5708
    c: Tangent(g90,g89) = -1.5708
    c: Tangent(g91,g89) = 1.5708
    c: Vertical(g90)
    c: DistanceY(g89,g88) = 66
    c: DistanceX(g89,g89) = 3
    c: Tangent(g92,g95) = 1.5708
    c: Tangent(g92,g94) = -1.5708
    c: Tangent(g94,g93) = -1.5708
    c: Tangent(g95,g93) = 1.5708
    c: Vertical(g94)
    c: DistanceY(g93,g92) = 66
    c: DistanceX(g93,g93) = 3
    c: DistanceX(g88,g92) = 6
    c: Tangent(g96,g99) = 1.5708
    c: Tangent(g96,g98) = -1.5708
    c: Tangent(g98,g97) = -1.5708
    c: Tangent(g99,g97) = 1.5708
    c: Vertical(g98)
    c: DistanceY(g97,g96) = 66
    c: DistanceX(g97,g97) = 3
    c: Tangent(g100,g103) = 1.5708
    c: Tangent(g100,g102) = -1.5708
    c: Tangent(g102,g101) = -1.5708
    c: Tangent(g103,g101) = 1.5708
    c: Vertical(g102)
    c: DistanceY(g101,g100) = 66
    c: DistanceX(g101,g101) = 3
    c: DistanceX(g96,g100) = 6
    c: DistanceX(g92,g96) = 12
    c: DistanceX(g84,g88) = 12
    c: Symmetric(g72,g73,g-1)
    c: Symmetric(g76,g77,g-1)
    c: Symmetric(g80,g81,g-1)
    c: Symmetric(g84,g85,g-1)
    c: Symmetric(g88,g89,g-1)
    c: Symmetric(g93,g92,g-1)
    c: Symmetric(g97,g96,g-1)
    c: Symmetric(g100,g101,g-1)
    c: Tangent(g104,g107) = 1.5708
    c: Tangent(g104,g106) = -1.5708
    c: Tangent(g106,g105) = -1.5708
    c: Tangent(g107,g105) = 1.5708
    c: Vertical(g106)
    c: DistanceY(g105,g104) = 66
    c: DistanceX(g105,g105) = 3
    c: Tangent(g108,g111) = 1.5708
    c: Tangent(g108,g110) = -1.5708
    c: Tangent(g110,g109) = -1.5708
    c: Tangent(g111,g109) = 1.5708
    c: Vertical(g110)
    c: DistanceY(g109,g108) = 66
    c: DistanceX(g109,g109) = 3
    c: DistanceX(g104,g108) = 6
    c: Symmetric(g104,g105,g-1)
    c: Symmetric(g108,g109,g-1)
    c: Tangent(g112,g115) = 1.5708
    c: Tangent(g112,g114) = -1.5708
    c: Tangent(g114,g113) = -1.5708
    c: Tangent(g115,g113) = 1.5708
    c: Vertical(g114)
    c: DistanceY(g113,g112) = 66
    c: DistanceX(g113,g113) = 3
    c: Tangent(g116,g119) = 1.5708
    c: Tangent(g116,g118) = -1.5708
    c: Tangent(g118,g117) = -1.5708
    c: Tangent(g119,g117) = 1.5708
    c: Vertical(g118)
    c: DistanceY(g117,g116) = 66
    c: DistanceX(g117,g117) = 3
    c: DistanceX(g112,g116) = 6
    c: Symmetric(g112,g113,g-1)
    c: Symmetric(g116,g117,g-1)
    c: DistanceX(g108,g112) = 12
    c: Coincident(g120,g121)
    c: Coincident(g121,g122)
    c: Coincident(g122,g123)
    c: Coincident(g123,g120)
    c: Horizontal(g120)
    c: Horizontal(g122)
    c: Vertical(g123)
    c: DistanceX(g122,g122) = 10
    c: DistanceY(g121,g121) = 100
    c: Symmetric(g121,g120,g-1)
    c: Coincident(g124,g125)
    c: Coincident(g125,g126)
    c: Coincident(g126,g127)
    c: Coincident(g127,g124)
    c: Horizontal(g124)
    c: Horizontal(g126)
    c: Vertical(g127)
    c: DistanceX(g126,g126) = 2
    c: DistanceY(g125,g125) = 20
    c: DistanceX(g121,g126) = 0
    c: Coincident(g128,g129)
    c: Coincident(g129,g130)
    c: Coincident(g130,g131)
    c: Coincident(g131,g128)
    c: Horizontal(g128)
    c: Horizontal(g130)
    c: Vertical(g131)
    c: DistanceY(g129,g129) = 20
    c: DistanceX(g128,g128) = 2
    c: DistanceX(g129,g122) = 0
    c: Symmetric(g128,g129,g-1)
    c: Symmetric(g124,g125,g-1)
    c: DistanceX(g120,g33) = 10
    c: Coincident(g132,g133)
    c: Coincident(g133,g134)
    c: Coincident(g134,g135)
    c: Coincident(g135,g132)
    c: Horizontal(g132)
    c: Horizontal(g134)
    c: Vertical(g133)
    c: Vertical(g135)
    c: DistanceX(g132,g132) = 5
    c: DistanceY(g133,g133) = 2
    c: DistanceX(g132,g121) = 2.5
    c: DistanceY(g132,g121) = 0
    c: Coincident(g136,g137)
    c: Coincident(g137,g138)
    c: Coincident(g138,g139)
    c: Coincident(g139,g136)
    c: Horizontal(g136)
    c: Horizontal(g138)
    c: Vertical(g137)
    c: Vertical(g139)
    c: DistanceY(g137,g137) = 2
    c: DistanceX(g136,g136) = 5
    c: DistanceY(g120,g137) = 0
    c: DistanceX(g137,g120) = 2.5
    c: Coincident(g140,g141)
    c: Coincident(g141,g142)
    c: Coincident(g142,g143)
    c: Coincident(g143,g140)
    c: Horizontal(g140)
    c: Horizontal(g142)
    c: Vertical(g141)
    c: Vertical(g143)
    c: DistanceY(g141,g141) = 10
    c: DistanceX(g140,g140) = 276
    c: DistanceX(g142,g33) = 1.5
    c: DistanceY(g33,g142) = 10
    c: Coincident(g144,g145)
    c: Coincident(g145,g146)
    c: Coincident(g146,g147)
    c: Coincident(g147,g144)
    c: Horizontal(g144)
    c: Horizontal(g146)
    c: Vertical(g145)
    c: Vertical(g147)
    c: DistanceY(g145,g145) = 5
    c: DistanceX(g146,g146) = 2
    c: DistanceX(g142,g146) = 2
    c: DistanceY(g142,g146) = 2.5
    c: Coincident(g148,g149)
    c: Coincident(g149,g150)
    c: Coincident(g150,g151)
    c: Coincident(g151,g148)
    c: Horizontal(g148)
    c: Horizontal(g150)
    c: Vertical(g149)
    c: Vertical(g151)
    c: Coincident(g152,g153)
    c: Coincident(g153,g154)
    c: Coincident(g154,g155)
    c: Coincident(g155,g152)
    c: Horizontal(g152)
    c: Horizontal(g154)
    c: Vertical(g153)
    c: Vertical(g155)
    c: DistanceY(g153,g153) = 2
    c: DistanceY(g149,g149) = 2
    c: DistanceX(g152,g152) = 20
    c: DistanceX(g148,g148) = 20
    c: DistanceY(g148,g142) = 0
    c: DistanceY(g140,g154) = 0
    c: DistanceX(g142,g148) = 40
    c: DistanceX(g140,g154) = 40
    c: Coincident(g156,g157)
    c: Coincident(g157,g158)
    c: Coincident(g158,g159)
    c: Coincident(g159,g156)
    c: Horizontal(g156)
    c: Horizontal(g158)
    c: Vertical(g157)
    c: Vertical(g159)
    c: DistanceX(g156,g156) = 2
    c: DistanceY(g159,g159) = 5
    c: DistanceX(g157,g141) = 2
    c: DistanceY(g141,g157) = 2.5
    c: Coincident(g160,g161)
    c: Coincident(g161,g162)
    c: Coincident(g162,g163)
    c: Coincident(g163,g160)
    c: Horizontal(g160)
    c: Horizontal(g162)
    c: Vertical(g161)
    c: Vertical(g163)
    c: DistanceY(g161,g161) = 2
    c: DistanceX(g160,g160) = 20
    c: DistanceX(g161,g140) = 40
    c: DistanceY(g140,g161) = 0
    c: Coincident(g164,g165)
    c: Coincident(g165,g166)
    c: Coincident(g166,g167)
    c: Coincident(g167,g164)
    c: Horizontal(g164)
    c: Horizontal(g166)
    c: Vertical(g165)
    c: Vertical(g167)
    c: DistanceY(g165,g165) = 2
    c: DistanceX(g166,g166) = 20
    c: DistanceY(g164,g141) = 0
    c: DistanceX(g164,g141) = 40
    c: Coincident(g168,g169)
    c: Coincident(g169,g170)
    c: Coincident(g170,g171)
    c: Coincident(g171,g168)
    c: Horizontal(g168)
    c: Horizontal(g170)
    c: Vertical(g169)
    c: Vertical(g171)
    c: DistanceX(g170,g170) = 4
    c: DistanceY(g171,g171) = 54.5
    c: DistanceX(g169,g121) = 1
    c: DistanceY(g121,g169) = 10
    c: Coincident(g172,g173)
    c: Coincident(g173,g174)
    c: Coincident(g174,g175)
    c: Coincident(g175,g172)
    c: Horizontal(g172)
    c: Horizontal(g174)
    c: Vertical(g173)
    c: Vertical(g175)
    c: DistanceX(g174,g174) = 2
    c: DistanceY(g173,g173) = 43
    c: DistanceY(g170,g173) = 5
    c: DistanceX(g173,g170) = 0
    c: DistanceY(g52,g54) = 60
FEATURE [PartDesign::Pad] Pad
  Direction = (1,1,1)
  Length = 0
  Length2 = 100
  Profile = -> Sketch
  Type = 0
FEATURE [PartDesign::Body] Body
  Group = -> [Sketch,Pad]
  Origin = -> Origin
  Tip = -> Pad
